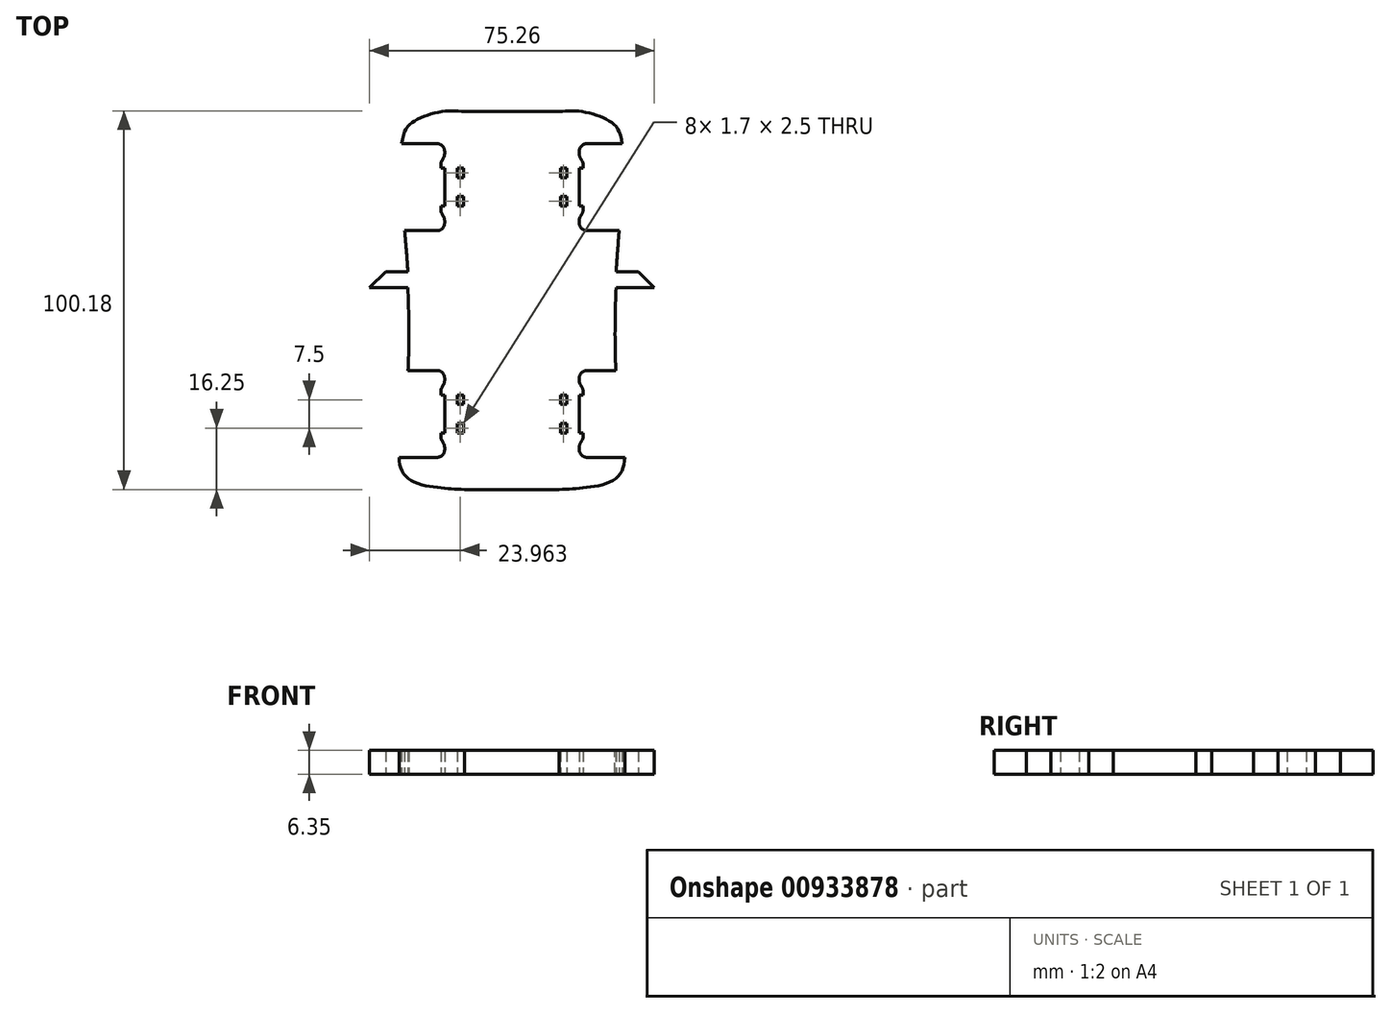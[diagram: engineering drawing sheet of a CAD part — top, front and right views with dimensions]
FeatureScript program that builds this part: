
annotation { "Feature Type Name" : "Feature", "Feature Type Description" : "" }
export const myFeature = defineFeature(function(context is Context, id is Id, definition is map)
    precondition{}
    {
        {
            var Q0;
            Q0=qCreatedBy(makeId("Top.planeOp"),FACE);
            var sketch = newSketch(context, id + "F0", { "sketchPlane" : qUnion([Q0])});
            skLineSegment(sketch, "E0.bottom", {"start": v(45, 50) * mm, "end": v(-45, 50) * mm, "construction": true});
            skLineSegment(sketch, "E0.top", {"start": v(45, -50) * mm, "end": v(-45, -50) * mm, "construction": true});
            skLineSegment(sketch, "E0.left", {"start": v(45, 50) * mm, "end": v(45, -50) * mm, "construction": true});
            skLineSegment(sketch, "E0.right", {"start": v(-45, 50) * mm, "end": v(-45, -50) * mm, "construction": true});
            skPoint(sketch, "E0.middle", {"position": v(0, 0) * mm});
            skSolve(sketch);
        }
        {
            var Q0;
            Q0=qCreatedBy(makeId("Top.planeOp"),FACE);
            var sketch = newSketch(context, id + "F1", { "sketchPlane" : qUnion([Q0])});
            skLineSegment(sketch, "E1", {"start": v(0, 50) * mm, "end": v(0, -50) * mm, "construction": true});
            skLineSegment(sketch, "E2", {"start": v(-27.54, 7.57) * mm, "end": v(-33.43, 7.57) * mm});
            skLineSegment(sketch, "E3", {"start": v(-33.43, 7.57) * mm, "end": v(-37.63, 3.38) * mm});
            skLineSegment(sketch, "E4", {"start": v(-37.63, 3.38) * mm, "end": v(-27.54, 3.38) * mm});
            skLineSegment(sketch, "E5", {"start": v(-12.5, 50) * mm, "end": v(12.5, 50) * mm});
            skFitSpline(sketch, "E6", {"points": [v(-12.5, 50) * mm, v(-18.52, 50) * mm, v(-25.51, 47.65) * mm, v(-28.77, 43.45) * mm, v(-28.77, 23.42) * mm, v(-27.54, 7.57) * mm], "startDerivative": vector(-37.57, 3.04) * mm, "endDerivative": vector(3.1, -57.79) * mm});
            skLineSegment(sketch, "E7", {"start": v(-12.5, -50) * mm, "end": v(12.5, -50) * mm});
            skFitSpline(sketch, "E8", {"points": [v(-27.54, 3.38) * mm, v(-27.54, -19.92) * mm, v(-28.72, -31.37) * mm, v(-29.9, -40.93) * mm, v(-27.54, -47.03) * mm, v(-19.35, -49.51) * mm, v(-12.5, -50) * mm], "startDerivative": vector(4.98, -107.6) * mm, "endDerivative": vector(53, -1.7) * mm});
            skLineSegment(sketch, "E9.MirrorCS", {"start": v(12.5, 50) * mm, "end": v(-12.5, 50) * mm});
            skFitSpline(sketch, "E10.MirrorCS", {"points": [v(12.5, 50) * mm, v(18.52, 50) * mm, v(25.51, 47.65) * mm, v(28.77, 43.45) * mm, v(28.77, 23.42) * mm, v(27.54, 7.57) * mm], "startDerivative": vector(37.57, 3.04) * mm, "endDerivative": vector(-3.1, -57.79) * mm});
            skLineSegment(sketch, "E11.MirrorCS", {"start": v(37.63, 3.38) * mm, "end": v(27.54, 3.38) * mm});
            skLineSegment(sketch, "E12.MirrorCS", {"start": v(27.54, 7.57) * mm, "end": v(33.43, 7.57) * mm});
            skLineSegment(sketch, "E13.MirrorCS", {"start": v(33.43, 7.57) * mm, "end": v(37.63, 3.38) * mm});
            skFitSpline(sketch, "E14.MirrorCS", {"points": [v(27.54, 3.38) * mm, v(27.54, -19.92) * mm, v(28.72, -31.37) * mm, v(29.9, -40.93) * mm, v(27.54, -47.03) * mm, v(19.35, -49.51) * mm, v(12.5, -50) * mm], "startDerivative": vector(-4.98, -107.6) * mm, "endDerivative": vector(-53, -1.7) * mm});
            skLineSegment(sketch, "E15.bottom", {"start": v(32.82, 18.5) * mm, "end": v(19.82, 18.5) * mm});
            skLineSegment(sketch, "E15.top", {"start": v(32.82, 41.5) * mm, "end": v(19.82, 41.5) * mm});
            skLineSegment(sketch, "E15.left", {"start": v(34.82, 20.5) * mm, "end": v(34.82, 39.5) * mm});
            skLineSegment(sketch, "E15.right", {"start": v(17.82, 20.5) * mm, "end": v(17.82, 21.23) * mm});
            skPoint(sketch, "E15.middle", {"position": v(11.03, 30) * mm});
            skLineSegment(sketch, "E16.bottom", {"start": v(14.52, 27.5) * mm, "end": v(12.82, 27.5) * mm});
            skLineSegment(sketch, "E16.top", {"start": v(14.52, 25) * mm, "end": v(12.82, 25) * mm});
            skLineSegment(sketch, "E16.left", {"start": v(14.52, 27.5) * mm, "end": v(14.52, 25) * mm});
            skLineSegment(sketch, "E16.right", {"start": v(12.82, 27.5) * mm, "end": v(12.82, 25) * mm});
            skPoint(sketch, "E16.middle", {"position": v(13.67, 26.25) * mm});
            skLineSegment(sketch, "E17.bottom", {"start": v(12.82, 35) * mm, "end": v(14.52, 35) * mm});
            skLineSegment(sketch, "E17.top", {"start": v(12.82, 32.5) * mm, "end": v(14.52, 32.5) * mm});
            skLineSegment(sketch, "E17.left", {"start": v(12.82, 35) * mm, "end": v(12.82, 32.5) * mm});
            skLineSegment(sketch, "E17.right", {"start": v(14.52, 35) * mm, "end": v(14.52, 32.5) * mm});
            skPoint(sketch, "E17.middle", {"position": v(13.67, 33.75) * mm});
            skLineSegment(sketch, "E18", {"start": v(13.67, 33.75) * mm, "end": v(13.67, 26.25) * mm, "construction": true});
            skLineSegment(sketch, "E19", {"start": v(13.67, 30) * mm, "end": v(11.03, 30) * mm, "construction": true});
            skLineSegment(sketch, "E20.bottom", {"start": v(26.07, 19) * mm, "end": v(19.07, 19) * mm, "construction": true});
            skLineSegment(sketch, "E20.top", {"start": v(26.07, 41) * mm, "end": v(19.07, 41) * mm, "construction": true});
            skLineSegment(sketch, "E20.left", {"start": v(26.07, 19) * mm, "end": v(26.07, 41) * mm, "construction": true});
            skLineSegment(sketch, "E20.right", {"start": v(19.07, 19) * mm, "end": v(19.07, 41) * mm, "construction": true});
            skPoint(sketch, "E20.middle", {"position": v(22.57, 30) * mm});
            skPoint(sketch, "E21.visualSharp", {"position": v(17.82, 18.5) * mm});
            skArc(sketch, "E21.filletArc", {"start": v(17.82, 20.5) * mm, "mid": v(18.4, 19.09) * mm, "end": v(19.82, 18.5) * mm});
            skPoint(sketch, "E22.visualSharp", {"position": v(17.82, 41.5) * mm});
            skArc(sketch, "E22.filletArc", {"start": v(19.82, 41.5) * mm, "mid": v(18.4, 40.91) * mm, "end": v(17.82, 39.5) * mm});
            skPoint(sketch, "E23.visualSharp", {"position": v(34.82, 41.5) * mm});
            skArc(sketch, "E23.filletArc", {"start": v(34.82, 39.5) * mm, "mid": v(34.23, 40.91) * mm, "end": v(32.82, 41.5) * mm});
            skPoint(sketch, "E24.visualSharp", {"position": v(34.82, 18.5) * mm});
            skArc(sketch, "E24.filletArc", {"start": v(32.82, 18.5) * mm, "mid": v(34.23, 19.09) * mm, "end": v(34.82, 20.5) * mm});
            skLineSegment(sketch, "E25.bottom", {"start": v(17.82, 25) * mm, "end": v(18.82, 25) * mm});
            skLineSegment(sketch, "E25.right", {"start": v(18.82, 25) * mm, "end": v(18.82, 24.04) * mm});
            skPoint(sketch, "E25.middle", {"position": v(18.32, 24.25) * mm});
            skLineSegment(sketch, "E26", {"start": v(18.55, 23.04) * mm, "end": v(18.08, 22.23) * mm});
            skPoint(sketch, "E27.visualSharp", {"position": v(18.82, 23.5) * mm});
            skArc(sketch, "E27.filletArc", {"start": v(18.55, 23.04) * mm, "mid": v(18.75, 23.52) * mm, "end": v(18.82, 24.04) * mm});
            skArc(sketch, "E28.filletArc", {"start": v(18.08, 22.23) * mm, "mid": v(17.88, 21.75) * mm, "end": v(17.82, 21.23) * mm});
            skLineSegment(sketch, "E29", {"start": v(17.82, 25) * mm, "end": v(17.82, 30) * mm});
            skArc(sketch, "E30.MirrorCS", {"start": v(18.08, 37.77) * mm, "mid": v(17.88, 38.25) * mm, "end": v(17.82, 38.77) * mm});
            skLineSegment(sketch, "E31.MirrorCS", {"start": v(17.82, 39.5) * mm, "end": v(17.82, 38.77) * mm});
            skLineSegment(sketch, "E32.MirrorCS", {"start": v(18.55, 36.96) * mm, "end": v(18.08, 37.77) * mm});
            skPoint(sketch, "E33.MirrorP", {"position": v(18.82, 36.5) * mm});
            skArc(sketch, "E34.MirrorCS", {"start": v(18.55, 36.96) * mm, "mid": v(18.75, 36.48) * mm, "end": v(18.82, 35.96) * mm});
            skLineSegment(sketch, "E35.MirrorCS", {"start": v(18.82, 35) * mm, "end": v(18.82, 35.96) * mm});
            skLineSegment(sketch, "E36.MirrorCS", {"start": v(17.82, 35) * mm, "end": v(18.82, 35) * mm});
            skLineSegment(sketch, "E37.MirrorCS", {"start": v(17.82, 35) * mm, "end": v(17.82, 30) * mm});
            skLineSegment(sketch, "E38.MirrorCS", {"start": v(-14.52, 27.5) * mm, "end": v(-14.52, 25) * mm});
            skLineSegment(sketch, "E39.MirrorCS", {"start": v(-12.82, 35) * mm, "end": v(-14.52, 35) * mm});
            skArc(sketch, "E40.MirrorCS", {"start": v(-18.08, 22.23) * mm, "mid": v(-17.88, 21.75) * mm, "end": v(-17.82, 21.23) * mm});
            skLineSegment(sketch, "E41.MirrorCS", {"start": v(-14.52, 25) * mm, "end": v(-12.82, 25) * mm});
            skLineSegment(sketch, "E42.MirrorCS", {"start": v(-14.52, 27.5) * mm, "end": v(-12.82, 27.5) * mm});
            skArc(sketch, "E43.MirrorCS", {"start": v(-18.55, 23.04) * mm, "mid": v(-18.75, 23.52) * mm, "end": v(-18.82, 24.04) * mm});
            skLineSegment(sketch, "E44.MirrorCS", {"start": v(-12.82, 32.5) * mm, "end": v(-14.52, 32.5) * mm});
            skLineSegment(sketch, "E45.MirrorCS", {"start": v(-17.82, 25) * mm, "end": v(-18.82, 25) * mm});
            skLineSegment(sketch, "E46.MirrorCS", {"start": v(-14.52, 35) * mm, "end": v(-14.52, 32.5) * mm});
            skLineSegment(sketch, "E47.MirrorCS", {"start": v(-18.55, 23.04) * mm, "end": v(-18.08, 22.23) * mm});
            skLineSegment(sketch, "E48.MirrorCS", {"start": v(-12.82, 27.5) * mm, "end": v(-12.82, 25) * mm});
            skLineSegment(sketch, "E49.MirrorCS", {"start": v(-18.82, 25) * mm, "end": v(-18.82, 24.04) * mm});
            skLineSegment(sketch, "E50.MirrorCS", {"start": v(-12.82, 35) * mm, "end": v(-12.82, 32.5) * mm});
            skArc(sketch, "E51.MirrorCS", {"start": v(-19.82, 41.5) * mm, "mid": v(-18.4, 40.91) * mm, "end": v(-17.82, 39.5) * mm});
            skLineSegment(sketch, "E52.MirrorCS", {"start": v(-17.82, 20.5) * mm, "end": v(-17.82, 21.23) * mm});
            skLineSegment(sketch, "E53.MirrorCS", {"start": v(-17.82, 35) * mm, "end": v(-18.82, 35) * mm});
            skArc(sketch, "E54.MirrorCS", {"start": v(-17.82, 20.5) * mm, "mid": v(-18.4, 19.09) * mm, "end": v(-19.82, 18.5) * mm});
            skPoint(sketch, "E55.MirrorP", {"position": v(-13.67, 33.75) * mm});
            skPoint(sketch, "E56.MirrorP", {"position": v(-13.67, 26.25) * mm});
            skPoint(sketch, "E57.MirrorP", {"position": v(-18.32, 24.25) * mm});
            skArc(sketch, "E58.MirrorCS", {"start": v(-18.08, 37.77) * mm, "mid": v(-17.88, 38.25) * mm, "end": v(-17.82, 38.77) * mm});
            skArc(sketch, "E59.MirrorCS", {"start": v(-18.55, 36.96) * mm, "mid": v(-18.75, 36.48) * mm, "end": v(-18.82, 35.96) * mm});
            skLineSegment(sketch, "E60.MirrorCS", {"start": v(-17.82, 39.5) * mm, "end": v(-17.82, 38.77) * mm});
            skLineSegment(sketch, "E61.MirrorCS", {"start": v(-18.82, 35) * mm, "end": v(-18.82, 35.96) * mm});
            skLineSegment(sketch, "E62.MirrorCS", {"start": v(-18.55, 36.96) * mm, "end": v(-18.08, 37.77) * mm});
            skPoint(sketch, "E63.MirrorP", {"position": v(-18.82, 23.5) * mm});
            skArc(sketch, "E64.MirrorCS", {"start": v(-34.82, 39.5) * mm, "mid": v(-34.23, 40.91) * mm, "end": v(-32.82, 41.5) * mm});
            skLineSegment(sketch, "E65.MirrorCS", {"start": v(-13.67, 30) * mm, "end": v(-11.03, 30) * mm, "construction": true});
            skArc(sketch, "E66.MirrorCS", {"start": v(-32.82, 18.5) * mm, "mid": v(-34.23, 19.09) * mm, "end": v(-34.82, 20.5) * mm});
            skPoint(sketch, "E67.MirrorP", {"position": v(-22.57, 30) * mm});
            skLineSegment(sketch, "E68.MirrorCS", {"start": v(-34.82, 20.5) * mm, "end": v(-34.82, 39.5) * mm});
            skLineSegment(sketch, "E69.MirrorCS", {"start": v(-26.07, 41) * mm, "end": v(-19.07, 41) * mm, "construction": true});
            skLineSegment(sketch, "E70.MirrorCS", {"start": v(-32.82, 41.5) * mm, "end": v(-19.82, 41.5) * mm});
            skLineSegment(sketch, "E71.MirrorCS", {"start": v(-13.67, 33.75) * mm, "end": v(-13.67, 26.25) * mm, "construction": true});
            skLineSegment(sketch, "E72.MirrorCS", {"start": v(-17.82, 25) * mm, "end": v(-17.82, 30) * mm});
            skPoint(sketch, "E73.MirrorP", {"position": v(-34.82, 41.5) * mm});
            skLineSegment(sketch, "E74.MirrorCS", {"start": v(-17.82, 35) * mm, "end": v(-17.82, 30) * mm});
            skLineSegment(sketch, "E75.MirrorCS", {"start": v(-19.07, 19) * mm, "end": v(-19.07, 41) * mm, "construction": true});
            skPoint(sketch, "E76.MirrorP", {"position": v(-11.03, 30) * mm});
            skPoint(sketch, "E77.MirrorP", {"position": v(-34.82, 18.5) * mm});
            skLineSegment(sketch, "E78.MirrorCS", {"start": v(-26.07, 19) * mm, "end": v(-19.07, 19) * mm, "construction": true});
            skPoint(sketch, "E79.MirrorP", {"position": v(-18.82, 36.5) * mm});
            skLineSegment(sketch, "E80.MirrorCS", {"start": v(-26.07, 19) * mm, "end": v(-26.07, 41) * mm, "construction": true});
            skPoint(sketch, "E81.MirrorP", {"position": v(-17.82, 41.5) * mm});
            skLineSegment(sketch, "E82.MirrorCS", {"start": v(-32.82, 18.5) * mm, "end": v(-19.82, 18.5) * mm});
            skPoint(sketch, "E83.MirrorP", {"position": v(-17.82, 18.5) * mm});
            skLineSegment(sketch, "E84.MirrorCS", {"start": v(18.82, -25) * mm, "end": v(18.82, -24.04) * mm});
            skArc(sketch, "E85.MirrorCS", {"start": v(18.08, -37.77) * mm, "mid": v(17.88, -38.25) * mm, "end": v(17.82, -38.77) * mm});
            skLineSegment(sketch, "E86.MirrorCS", {"start": v(-18.82, -35) * mm, "end": v(-18.82, -35.96) * mm});
            skLineSegment(sketch, "E87.MirrorCS", {"start": v(18.55, -36.96) * mm, "end": v(18.08, -37.77) * mm});
            skLineSegment(sketch, "E88.MirrorCS", {"start": v(17.82, -39.5) * mm, "end": v(17.82, -38.77) * mm});
            skLineSegment(sketch, "E89.MirrorCS", {"start": v(12.82, -35) * mm, "end": v(12.82, -32.5) * mm});
            skLineSegment(sketch, "E90.MirrorCS", {"start": v(14.52, -35) * mm, "end": v(14.52, -32.5) * mm});
            skArc(sketch, "E91.MirrorCS", {"start": v(18.08, -22.23) * mm, "mid": v(17.88, -21.75) * mm, "end": v(17.82, -21.23) * mm});
            skLineSegment(sketch, "E92.MirrorCS", {"start": v(12.82, -35) * mm, "end": v(14.52, -35) * mm});
            skLineSegment(sketch, "E93.MirrorCS", {"start": v(-18.55, -23.04) * mm, "end": v(-18.08, -22.23) * mm});
            skLineSegment(sketch, "E94.MirrorCS", {"start": v(17.82, -20.5) * mm, "end": v(17.82, -21.23) * mm});
            skLineSegment(sketch, "E95.MirrorCS", {"start": v(-18.82, -25) * mm, "end": v(-18.82, -24.04) * mm});
            skArc(sketch, "E96.MirrorCS", {"start": v(-18.55, -36.96) * mm, "mid": v(-18.75, -36.48) * mm, "end": v(-18.82, -35.96) * mm});
            skArc(sketch, "E97.MirrorCS", {"start": v(-18.08, -37.77) * mm, "mid": v(-17.88, -38.25) * mm, "end": v(-17.82, -38.77) * mm});
            skLineSegment(sketch, "E98.MirrorCS", {"start": v(-17.82, -35) * mm, "end": v(-18.82, -35) * mm});
            skLineSegment(sketch, "E99.MirrorCS", {"start": v(17.82, -25) * mm, "end": v(18.82, -25) * mm});
            skArc(sketch, "E100.MirrorCS", {"start": v(18.55, -23.04) * mm, "mid": v(18.75, -23.52) * mm, "end": v(18.82, -24.04) * mm});
            skLineSegment(sketch, "E101.MirrorCS", {"start": v(-17.82, -39.5) * mm, "end": v(-17.82, -38.77) * mm});
            skLineSegment(sketch, "E102.MirrorCS", {"start": v(18.55, -23.04) * mm, "end": v(18.08, -22.23) * mm});
            skArc(sketch, "E103.MirrorCS", {"start": v(18.55, -36.96) * mm, "mid": v(18.75, -36.48) * mm, "end": v(18.82, -35.96) * mm});
            skLineSegment(sketch, "E104.MirrorCS", {"start": v(18.82, -35) * mm, "end": v(18.82, -35.96) * mm});
            skLineSegment(sketch, "E105.MirrorCS", {"start": v(-18.55, -36.96) * mm, "end": v(-18.08, -37.77) * mm});
            skLineSegment(sketch, "E106.MirrorCS", {"start": v(12.82, -32.5) * mm, "end": v(14.52, -32.5) * mm});
            skPoint(sketch, "E107.MirrorP", {"position": v(13.67, -33.75) * mm});
            skLineSegment(sketch, "E108.MirrorCS", {"start": v(-12.82, -32.5) * mm, "end": v(-14.52, -32.5) * mm});
            skLineSegment(sketch, "E109.MirrorCS", {"start": v(-12.82, -27.5) * mm, "end": v(-12.82, -25) * mm});
            skLineSegment(sketch, "E110.MirrorCS", {"start": v(-14.52, -25) * mm, "end": v(-12.82, -25) * mm});
            skLineSegment(sketch, "E111.MirrorCS", {"start": v(-17.82, -20.5) * mm, "end": v(-17.82, -21.23) * mm});
            skLineSegment(sketch, "E112.MirrorCS", {"start": v(14.52, -27.5) * mm, "end": v(14.52, -25) * mm});
            skLineSegment(sketch, "E113.MirrorCS", {"start": v(-14.52, -35) * mm, "end": v(-14.52, -32.5) * mm});
            skArc(sketch, "E114.MirrorCS", {"start": v(-18.55, -23.04) * mm, "mid": v(-18.75, -23.52) * mm, "end": v(-18.82, -24.04) * mm});
            skLineSegment(sketch, "E115.MirrorCS", {"start": v(-12.82, -35) * mm, "end": v(-12.82, -32.5) * mm});
            skLineSegment(sketch, "E116.MirrorCS", {"start": v(-12.82, -35) * mm, "end": v(-14.52, -35) * mm});
            skLineSegment(sketch, "E117.MirrorCS", {"start": v(12.82, -27.5) * mm, "end": v(12.82, -25) * mm});
            skLineSegment(sketch, "E118.MirrorCS", {"start": v(14.52, -25) * mm, "end": v(12.82, -25) * mm});
            skLineSegment(sketch, "E119.MirrorCS", {"start": v(17.82, -35) * mm, "end": v(18.82, -35) * mm});
            skLineSegment(sketch, "E120.MirrorCS", {"start": v(-14.52, -27.5) * mm, "end": v(-14.52, -25) * mm});
            skLineSegment(sketch, "E121.MirrorCS", {"start": v(-14.52, -27.5) * mm, "end": v(-12.82, -27.5) * mm});
            skArc(sketch, "E122.MirrorCS", {"start": v(-18.08, -22.23) * mm, "mid": v(-17.88, -21.75) * mm, "end": v(-17.82, -21.23) * mm});
            skLineSegment(sketch, "E123.MirrorCS", {"start": v(-17.82, -25) * mm, "end": v(-18.82, -25) * mm});
            skLineSegment(sketch, "E124.MirrorCS", {"start": v(14.52, -27.5) * mm, "end": v(12.82, -27.5) * mm});
            skArc(sketch, "E125.MirrorCS", {"start": v(-34.82, -39.5) * mm, "mid": v(-34.23, -40.91) * mm, "end": v(-32.82, -41.5) * mm});
            skLineSegment(sketch, "E126.MirrorCS", {"start": v(13.67, -30) * mm, "end": v(11.03, -30) * mm, "construction": true});
            skLineSegment(sketch, "E127.MirrorCS", {"start": v(17.82, -25) * mm, "end": v(17.82, -30) * mm});
            skLineSegment(sketch, "E128.MirrorCS", {"start": v(13.67, -33.75) * mm, "end": v(13.67, -26.25) * mm, "construction": true});
            skArc(sketch, "E129.MirrorCS", {"start": v(17.82, -20.5) * mm, "mid": v(18.4, -19.09) * mm, "end": v(19.82, -18.5) * mm});
            skLineSegment(sketch, "E130.MirrorCS", {"start": v(-19.07, -19) * mm, "end": v(-19.07, -41) * mm, "construction": true});
            skPoint(sketch, "E131.MirrorP", {"position": v(-13.67, -26.25) * mm});
            skLineSegment(sketch, "E132.MirrorCS", {"start": v(-17.82, -35) * mm, "end": v(-17.82, -30) * mm});
            skArc(sketch, "E133.MirrorCS", {"start": v(19.82, -41.5) * mm, "mid": v(18.4, -40.91) * mm, "end": v(17.82, -39.5) * mm});
            skLineSegment(sketch, "E134.MirrorCS", {"start": v(19.07, -19) * mm, "end": v(19.07, -41) * mm, "construction": true});
            skLineSegment(sketch, "E135.MirrorCS", {"start": v(-17.82, -25) * mm, "end": v(-17.82, -30) * mm});
            skArc(sketch, "E136.MirrorCS", {"start": v(-17.82, -20.5) * mm, "mid": v(-18.4, -19.09) * mm, "end": v(-19.82, -18.5) * mm});
            skPoint(sketch, "E137.MirrorP", {"position": v(18.82, -23.5) * mm});
            skArc(sketch, "E138.MirrorCS", {"start": v(-19.82, -41.5) * mm, "mid": v(-18.4, -40.91) * mm, "end": v(-17.82, -39.5) * mm});
            skPoint(sketch, "E139.MirrorP", {"position": v(-13.67, -33.75) * mm});
            skLineSegment(sketch, "E140.MirrorCS", {"start": v(17.82, -35) * mm, "end": v(17.82, -30) * mm});
            skArc(sketch, "E141.MirrorCS", {"start": v(32.82, -18.5) * mm, "mid": v(34.23, -19.09) * mm, "end": v(34.82, -20.5) * mm});
            skPoint(sketch, "E142.MirrorP", {"position": v(13.67, -26.25) * mm});
            skArc(sketch, "E143.MirrorCS", {"start": v(34.82, -39.5) * mm, "mid": v(34.23, -40.91) * mm, "end": v(32.82, -41.5) * mm});
            skArc(sketch, "E144.MirrorCS", {"start": v(-32.82, -18.5) * mm, "mid": v(-34.23, -19.09) * mm, "end": v(-34.82, -20.5) * mm});
            skLineSegment(sketch, "E145.MirrorCS", {"start": v(-13.67, -33.75) * mm, "end": v(-13.67, -26.25) * mm, "construction": true});
            skPoint(sketch, "E146.MirrorP", {"position": v(18.32, -24.25) * mm});
            skLineSegment(sketch, "E147.MirrorCS", {"start": v(-13.67, -30) * mm, "end": v(-11.03, -30) * mm, "construction": true});
            skPoint(sketch, "E148.MirrorP", {"position": v(11.03, -30) * mm});
            skLineSegment(sketch, "E149.MirrorCS", {"start": v(26.07, -19) * mm, "end": v(26.07, -41) * mm, "construction": true});
            skPoint(sketch, "E150.MirrorP", {"position": v(-18.32, -24.25) * mm});
            skLineSegment(sketch, "E151.MirrorCS", {"start": v(32.82, -18.5) * mm, "end": v(19.82, -18.5) * mm});
            skLineSegment(sketch, "E152.MirrorCS", {"start": v(-34.82, -20.5) * mm, "end": v(-34.82, -39.5) * mm});
            skLineSegment(sketch, "E153.MirrorCS", {"start": v(32.82, -41.5) * mm, "end": v(19.82, -41.5) * mm});
            skLineSegment(sketch, "E154.MirrorCS", {"start": v(26.07, -41) * mm, "end": v(19.07, -41) * mm, "construction": true});
            skPoint(sketch, "E155.MirrorP", {"position": v(34.82, -18.5) * mm});
            skLineSegment(sketch, "E156.MirrorCS", {"start": v(26.07, -19) * mm, "end": v(19.07, -19) * mm, "construction": true});
            skLineSegment(sketch, "E157.MirrorCS", {"start": v(-26.07, -41) * mm, "end": v(-19.07, -41) * mm, "construction": true});
            skPoint(sketch, "E158.MirrorP", {"position": v(-18.82, -36.5) * mm});
            skPoint(sketch, "E159.MirrorP", {"position": v(17.82, -41.5) * mm});
            skPoint(sketch, "E160.MirrorP", {"position": v(-18.82, -23.5) * mm});
            skPoint(sketch, "E161.MirrorP", {"position": v(17.82, -18.5) * mm});
            skLineSegment(sketch, "E162.MirrorCS", {"start": v(-32.82, -41.5) * mm, "end": v(-19.82, -41.5) * mm});
            skLineSegment(sketch, "E163.MirrorCS", {"start": v(-26.07, -19) * mm, "end": v(-19.07, -19) * mm, "construction": true});
            skLineSegment(sketch, "E164.MirrorCS", {"start": v(-32.82, -18.5) * mm, "end": v(-19.82, -18.5) * mm});
            skPoint(sketch, "E165.MirrorP", {"position": v(22.57, -30) * mm});
            skPoint(sketch, "E166.MirrorP", {"position": v(-17.82, -18.5) * mm});
            skPoint(sketch, "E167.MirrorP", {"position": v(-34.82, -41.5) * mm});
            skPoint(sketch, "E168.MirrorP", {"position": v(-34.82, -18.5) * mm});
            skPoint(sketch, "E169.MirrorP", {"position": v(-11.03, -30) * mm});
            skLineSegment(sketch, "E170.MirrorCS", {"start": v(34.82, -20.5) * mm, "end": v(34.82, -39.5) * mm});
            skPoint(sketch, "E171.MirrorP", {"position": v(-17.82, -41.5) * mm});
            skLineSegment(sketch, "E172.MirrorCS", {"start": v(-26.07, -19) * mm, "end": v(-26.07, -41) * mm, "construction": true});
            skPoint(sketch, "E173.MirrorP", {"position": v(18.82, -36.5) * mm});
            skPoint(sketch, "E174.MirrorP", {"position": v(-22.57, -30) * mm});
            skPoint(sketch, "E175.MirrorP", {"position": v(34.82, -41.5) * mm});
            skSolve(sketch);
        }
        {
            var Q0;
            Q0=makeQuery(id+"F1.imprint","IMPRINT",FACE,{"disambiguationData":[TD([[makeQuery(id+"F1.imprint","IMPRINT",EDGE,{"derivedFrom":sQuery(id+"F1.wireOp",EDGE,"E2")}),1.0]])]});
            var Q1;
            Q1=makeQuery(id+"F1.imprint","IMPRINT",FACE,{"disambiguationData":[TD([[makeQuery(id+"F1.imprint","IMPRINT",EDGE,{"derivedFrom":sQuery(id+"F1.wireOp",EDGE,"E2")}),1.0]])]});
            var Q2;
            Q2=makeQuery(id+"FFzDFJW69ZhYbQy_1.merge.FwZItLE7f57oVm5_0.imprint","IMPRINT",FACE,{"disambiguationData":[TD([[makeQuery(id+"FFzDFJW69ZhYbQy_1.merge.FwZItLE7f57oVm5_0.imprint","IMPRINT",EDGE,{"derivedFrom":sQuery(id+"FFzDFJW69ZhYbQy_1.merge.FwZItLE7f57oVm5_0.wireOp",EDGE,"q6PWfxKt-3Lkw-Qjh8-70q7-Zbc5AiX1qyuv.bottom")}),1.0]])]});
            extrude(context, id + "F2", {"entities" : qUnion([Q0, Q1, Q2]), "depth" : 6.35 * mm, "offsetDistance" : 25 * mm});
        }
    });
